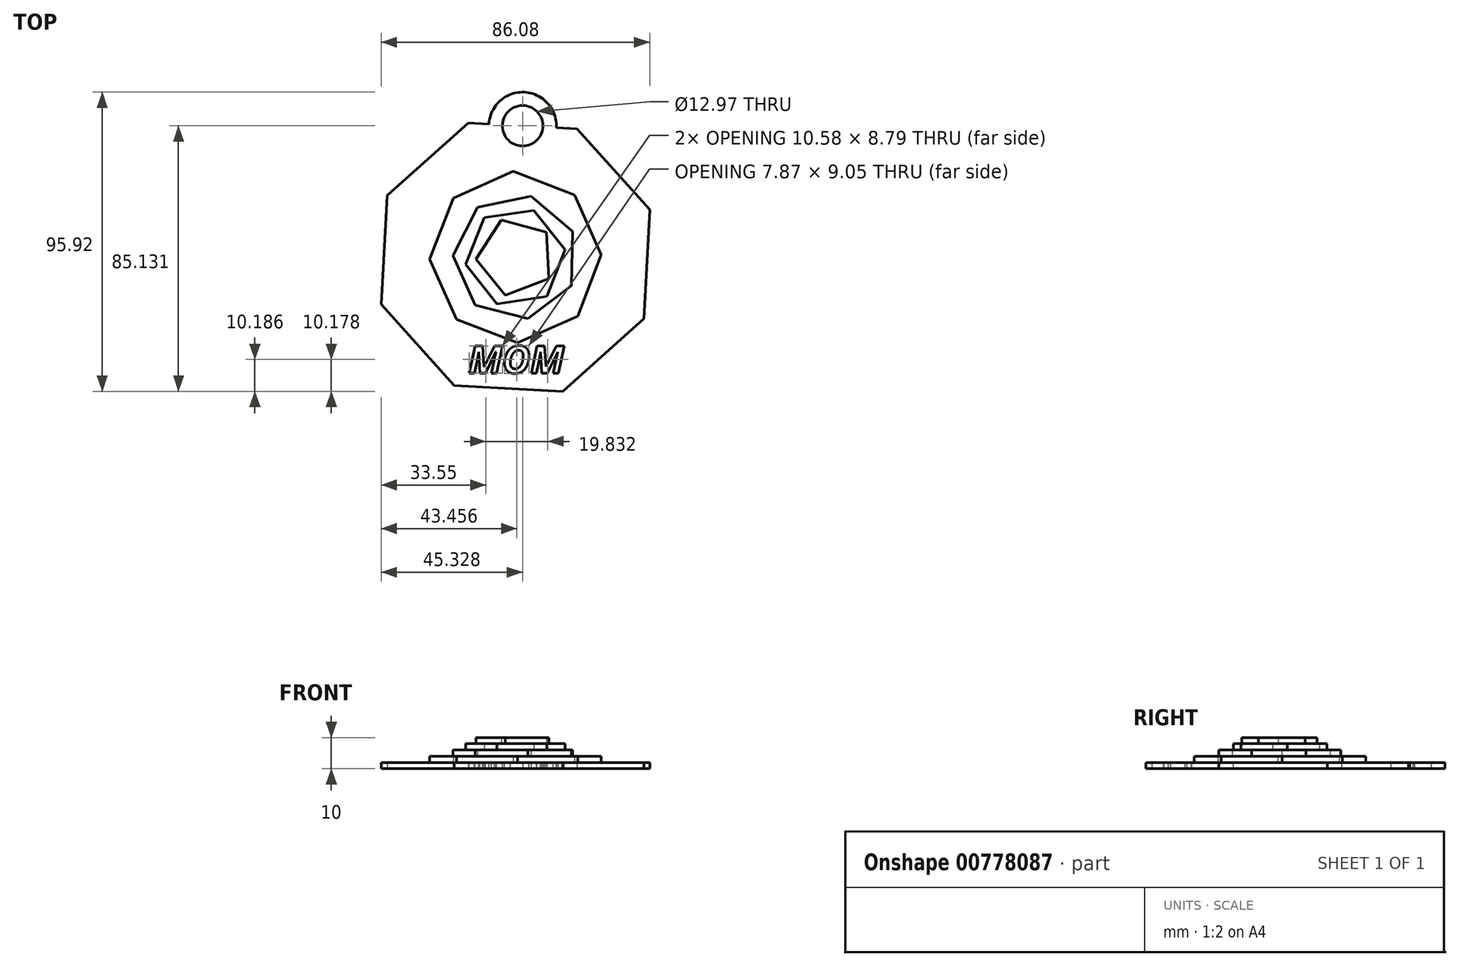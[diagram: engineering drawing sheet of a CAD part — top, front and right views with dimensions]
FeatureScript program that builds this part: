
annotation { "Feature Type Name" : "Feature", "Feature Type Description" : "" }
export const myFeature = defineFeature(function(context is Context, id is Id, definition is map)
    precondition{}
    {
        {
            var Q0;
            Q0=qCreatedBy(makeId("Top.planeOp"),FACE);
            var sketch = newSketch(context, id + "F0", { "sketchPlane" : qUnion([Q0])});
            skCircle(sketch, "E0.cCircle", {"center": v(0, 0) * mm, "radius": 42.15 * mm, "construction": true});
            skLineSegment(sketch, "E0.0", {"start": v(19.72, 41.14) * mm, "end": v(43.04, 15.15) * mm});
            skLineSegment(sketch, "E0.1", {"start": v(43.04, 15.15) * mm, "end": v(41.14, -19.72) * mm});
            skLineSegment(sketch, "E0.2", {"start": v(41.14, -19.72) * mm, "end": v(15.15, -43.04) * mm});
            skLineSegment(sketch, "E0.3", {"start": v(15.15, -43.04) * mm, "end": v(-19.72, -41.14) * mm});
            skLineSegment(sketch, "E0.4", {"start": v(-19.72, -41.14) * mm, "end": v(-43.04, -15.15) * mm});
            skLineSegment(sketch, "E0.5", {"start": v(-43.04, -15.15) * mm, "end": v(-41.14, 19.72) * mm});
            skLineSegment(sketch, "E0.6", {"start": v(-41.14, 19.72) * mm, "end": v(-15.15, 43.04) * mm});
            skLineSegment(sketch, "E0.7", {"start": v(-15.15, 43.04) * mm, "end": v(19.72, 41.14) * mm});
            skPoint(sketch, "E0.0.midPoint", {"position": v(31.38, 28.14) * mm});
            skSolve(sketch);
        }
        {
            var Q0;
            Q0=makeQuery(id+"F0.imprint","IMPRINT",FACE,{"disambiguationData":[TD([[makeQuery(id+"F0.imprint","IMPRINT",EDGE,{"derivedFrom":sQuery(id+"F0.wireOp",EDGE,"E0.0")}),-1.0]])]});
            extrude(context, id + "F1", {"entities" : qUnion([Q0]), "depth" : 2 * mm, "offsetDistance" : 25.4 * mm});
        }
        {
            var Q0;
            Q0=makeQuery(id+"F1.opExtrude","CAP_FACE",FACE,{"disambiguationData":[OSD([sQuery(id+"F0.wireOp",EDGE,"E0.0"),sQuery(id+"F0.wireOp",EDGE,"E0.1"),sQuery(id+"F0.wireOp",EDGE,"E0.2"),sQuery(id+"F0.wireOp",EDGE,"E0.3"),sQuery(id+"F0.wireOp",EDGE,"E0.4"),sQuery(id+"F0.wireOp",EDGE,"E0.5"),sQuery(id+"F0.wireOp",EDGE,"E0.6"),sQuery(id+"F0.wireOp",EDGE,"E0.7")])],"isStart":false});
            var sketch = newSketch(context, id + "F2", { "sketchPlane" : qUnion([Q0])});
            skCircle(sketch, "E1.cCircle", {"center": v(0, 0) * mm, "radius": 25.4 * mm, "construction": true});
            skLineSegment(sketch, "E1.0", {"start": v(-19.93, 18.95) * mm, "end": v(-0.7, 27.5) * mm});
            skLineSegment(sketch, "E1.1", {"start": v(-0.7, 27.5) * mm, "end": v(18.95, 19.93) * mm});
            skLineSegment(sketch, "E1.2", {"start": v(18.95, 19.93) * mm, "end": v(27.5, 0.7) * mm});
            skLineSegment(sketch, "E1.3", {"start": v(27.5, 0.7) * mm, "end": v(19.93, -18.95) * mm});
            skLineSegment(sketch, "E1.4", {"start": v(19.93, -18.95) * mm, "end": v(0.7, -27.5) * mm});
            skLineSegment(sketch, "E1.5", {"start": v(0.7, -27.5) * mm, "end": v(-18.95, -19.93) * mm});
            skLineSegment(sketch, "E1.6", {"start": v(-18.95, -19.93) * mm, "end": v(-27.5, -0.7) * mm});
            skLineSegment(sketch, "E1.7", {"start": v(-27.5, -0.7) * mm, "end": v(-19.93, 18.95) * mm});
            skPoint(sketch, "E1.0.midPoint", {"position": v(-10.31, 23.22) * mm});
            skSolve(sketch);
        }
        {
            var Q0;
            Q0=qSketchRegion(id+"F2",true);
            extrude(context, id + "F3", {"entities" : qUnion([Q0]), "operationType" : NewBodyOperationType.ADD, "depth" : 2 * mm, "offsetDistance" : 25.4 * mm});
        }
        {
            var Q0;
            Q0=makeQuery(id+"F3.opExtrude","CAP_FACE",FACE,{"disambiguationData":[OSD([sQuery(id+"F2.wireOp",EDGE,"E1.0"),sQuery(id+"F2.wireOp",EDGE,"E1.1"),sQuery(id+"F2.wireOp",EDGE,"E1.2"),sQuery(id+"F2.wireOp",EDGE,"E1.3"),sQuery(id+"F2.wireOp",EDGE,"E1.4"),sQuery(id+"F2.wireOp",EDGE,"E1.5"),sQuery(id+"F2.wireOp",EDGE,"E1.6"),sQuery(id+"F2.wireOp",EDGE,"E1.7")])],"isStart":false});
            var sketch = newSketch(context, id + "F4", { "sketchPlane" : qUnion([Q0])});
            skCircle(sketch, "E2.cCircle", {"center": v(0, 0) * mm, "radius": 18.1 * mm, "construction": true});
            skLineSegment(sketch, "E2.0", {"start": v(-20.08, 0.5) * mm, "end": v(-12.13, 16.02) * mm});
            skLineSegment(sketch, "E2.1", {"start": v(-12.13, 16.02) * mm, "end": v(4.96, 19.47) * mm});
            skLineSegment(sketch, "E2.2", {"start": v(4.96, 19.47) * mm, "end": v(18.32, 8.26) * mm});
            skLineSegment(sketch, "E2.3", {"start": v(18.32, 8.26) * mm, "end": v(17.87, -9.17) * mm});
            skLineSegment(sketch, "E2.4", {"start": v(17.87, -9.17) * mm, "end": v(3.97, -19.7) * mm});
            skLineSegment(sketch, "E2.5", {"start": v(3.97, -19.7) * mm, "end": v(-12.92, -15.39) * mm});
            skLineSegment(sketch, "E2.6", {"start": v(-12.92, -15.39) * mm, "end": v(-20.08, 0.5) * mm});
            skPoint(sketch, "E2.0.midPoint", {"position": v(-16.1, 8.26) * mm});
            skSolve(sketch);
        }
        {
            var Q0;
            Q0=qSketchRegion(id+"F4",true);
            extrude(context, id + "F5", {"entities" : qUnion([Q0]), "operationType" : NewBodyOperationType.ADD, "depth" : 2 * mm, "offsetDistance" : 25.4 * mm});
        }
        {
            var Q0;
            Q0=makeQuery(id+"F5.opExtrude","CAP_FACE",FACE,{"disambiguationData":[OSD([sQuery(id+"F4.wireOp",EDGE,"E2.0"),sQuery(id+"F4.wireOp",EDGE,"E2.1"),sQuery(id+"F4.wireOp",EDGE,"E2.2"),sQuery(id+"F4.wireOp",EDGE,"E2.3"),sQuery(id+"F4.wireOp",EDGE,"E2.4"),sQuery(id+"F4.wireOp",EDGE,"E2.5"),sQuery(id+"F4.wireOp",EDGE,"E2.6")])],"isStart":false});
            var sketch = newSketch(context, id + "F6", { "sketchPlane" : qUnion([Q0])});
            skSolve(sketch);
        }
        {
            var Q0;
            Q0=makeQuery(id+"F6.imprint","IMPRINT",FACE,{"disambiguationData":[TD([[makeQuery(id+"F6.imprint","IMPRINT",EDGE,{"derivedFrom":makeQuery(id+"F5.opExtrude","CAP_EDGE",EDGE,{"disambiguationData":[OSD([sQuery(id+"F4.wireOp",EDGE,"E2.0")])],"isStart":false})}),-1.0]])]});
            var sketch = newSketch(context, id + "F7", { "sketchPlane" : qUnion([Q0])});
            skCircle(sketch, "E3.cCircle", {"center": v(0, 0) * mm, "radius": 13.94 * mm, "construction": true});
            skLineSegment(sketch, "E3.0", {"start": v(-15.93, -2.36) * mm, "end": v(-10, 12.61) * mm});
            skLineSegment(sketch, "E3.1", {"start": v(-10, 12.61) * mm, "end": v(5.92, 14.97) * mm});
            skLineSegment(sketch, "E3.2", {"start": v(5.92, 14.97) * mm, "end": v(15.93, 2.36) * mm});
            skLineSegment(sketch, "E3.3", {"start": v(15.93, 2.36) * mm, "end": v(10, -12.61) * mm});
            skLineSegment(sketch, "E3.4", {"start": v(10, -12.61) * mm, "end": v(-5.92, -14.97) * mm});
            skLineSegment(sketch, "E3.5", {"start": v(-5.92, -14.97) * mm, "end": v(-15.93, -2.36) * mm});
            skPoint(sketch, "E3.0.midPoint", {"position": v(-12.97, 5.13) * mm});
            skSolve(sketch);
        }
        {
            var Q0;
            Q0=qSketchRegion(id+"F7",true);
            extrude(context, id + "F8", {"entities" : qUnion([Q0]), "operationType" : NewBodyOperationType.ADD, "depth" : 2 * mm, "offsetDistance" : 25.4 * mm});
        }
        {
            var Q0;
            Q0=makeQuery(id+"F8.opExtrude","CAP_FACE",FACE,{"disambiguationData":[OSD([sQuery(id+"F7.wireOp",EDGE,"E3.0"),sQuery(id+"F7.wireOp",EDGE,"E3.1"),sQuery(id+"F7.wireOp",EDGE,"E3.2"),sQuery(id+"F7.wireOp",EDGE,"E3.3"),sQuery(id+"F7.wireOp",EDGE,"E3.4"),sQuery(id+"F7.wireOp",EDGE,"E3.5")])],"isStart":false});
            var sketch = newSketch(context, id + "F9", { "sketchPlane" : qUnion([Q0])});
            skCircle(sketch, "E4.cCircle", {"center": v(0, 0) * mm, "radius": 10.29 * mm, "construction": true});
            skLineSegment(sketch, "E4.0", {"start": v(-12.7, -0.66) * mm, "end": v(-4.55, 11.88) * mm});
            skLineSegment(sketch, "E4.1", {"start": v(-4.55, 11.88) * mm, "end": v(9.89, 8) * mm});
            skLineSegment(sketch, "E4.2", {"start": v(9.89, 8) * mm, "end": v(10.66, -6.93) * mm});
            skLineSegment(sketch, "E4.3", {"start": v(10.66, -6.93) * mm, "end": v(-3.3, -12.28) * mm});
            skLineSegment(sketch, "E4.4", {"start": v(-3.3, -12.28) * mm, "end": v(-12.7, -0.66) * mm});
            skPoint(sketch, "E4.0.midPoint", {"position": v(-8.63, 5.6) * mm});
            skSolve(sketch);
        }
        {
            var Q0;
            Q0=qSketchRegion(id+"F9",true);
            extrude(context, id + "F10", {"entities" : qUnion([Q0]), "operationType" : NewBodyOperationType.ADD, "depth" : 2 * mm, "offsetDistance" : 25.4 * mm});
        }
        {
            var Q0;
            Q0=makeQuery(id+"F1.opExtrude","CAP_FACE",FACE,{"disambiguationData":[OSD([sQuery(id+"F0.wireOp",EDGE,"E0.0"),sQuery(id+"F0.wireOp",EDGE,"E0.1"),sQuery(id+"F0.wireOp",EDGE,"E0.2"),sQuery(id+"F0.wireOp",EDGE,"E0.3"),sQuery(id+"F0.wireOp",EDGE,"E0.4"),sQuery(id+"F0.wireOp",EDGE,"E0.5"),sQuery(id+"F0.wireOp",EDGE,"E0.6"),sQuery(id+"F0.wireOp",EDGE,"E0.7")])],"isStart":false});
            var sketch = newSketch(context, id + "F11", { "sketchPlane" : qUnion([Q0])});
            skCircle(sketch, "E5", {"center": v(2.29, 42.1) * mm, "radius": 10.8 * mm});
            skSolve(sketch);
        }
        {
            var Q0;
            Q0=qSketchRegion(id+"F11",true);
            extrude(context, id + "F12", {"entities" : qUnion([Q0]), "operationType" : NewBodyOperationType.ADD, "oppositeDirection" : true, "depth" : 2 * mm, "offsetDistance" : 25.4 * mm});
        }
        {
            var Q0;
            Q0=makeQuery(id+"F12.boolean.opBoolean","MERGE",FACE,{"derivedFrom":[makeQuery(id+"F1.opExtrude","CAP_FACE",FACE,{"disambiguationData":[OSD([sQuery(id+"F0.wireOp",EDGE,"E0.0"),sQuery(id+"F0.wireOp",EDGE,"E0.1"),sQuery(id+"F0.wireOp",EDGE,"E0.2"),sQuery(id+"F0.wireOp",EDGE,"E0.3"),sQuery(id+"F0.wireOp",EDGE,"E0.4"),sQuery(id+"F0.wireOp",EDGE,"E0.5"),sQuery(id+"F0.wireOp",EDGE,"E0.6"),sQuery(id+"F0.wireOp",EDGE,"E0.7")])],"isStart":false}),makeQuery(id+"F12.opExtrude","CAP_FACE",FACE,{"disambiguationData":[OSD([sQuery(id+"F11.wireOp",EDGE,"E5")])],"isStart":true})]});
            var sketch = newSketch(context, id + "F13", { "sketchPlane" : qUnion([Q0])});
            skCircle(sketch, "E6", {"center": v(2.29, 42.1) * mm, "radius": 6.48 * mm});
            skSolve(sketch);
        }
        {
            var Q0;
            Q0=qSketchRegion(id+"F13",true);
            extrude(context, id + "F14", {"entities" : qUnion([Q0]), "operationType" : NewBodyOperationType.REMOVE, "oppositeDirection" : true, "depth" : 25.4 * mm, "offsetDistance" : 25.4 * mm});
        }
        {
            var Q0;
            Q0=makeQuery(id+"F12.boolean.opBoolean","MERGE",FACE,{"derivedFrom":[makeQuery(id+"F1.opExtrude","CAP_FACE",FACE,{"disambiguationData":[OSD([sQuery(id+"F0.wireOp",EDGE,"E0.0"),sQuery(id+"F0.wireOp",EDGE,"E0.1"),sQuery(id+"F0.wireOp",EDGE,"E0.2"),sQuery(id+"F0.wireOp",EDGE,"E0.3"),sQuery(id+"F0.wireOp",EDGE,"E0.4"),sQuery(id+"F0.wireOp",EDGE,"E0.5"),sQuery(id+"F0.wireOp",EDGE,"E0.6"),sQuery(id+"F0.wireOp",EDGE,"E0.7")])],"isStart":false}),makeQuery(id+"F12.opExtrude","CAP_FACE",FACE,{"disambiguationData":[OSD([sQuery(id+"F11.wireOp",EDGE,"E5")])],"isStart":true})]});
            var sketch = newSketch(context, id + "F15", { "sketchPlane" : qUnion([Q0])});
            skText(sketch, "E7", { "text": "MOM", "fontName": "OpenSans-BoldItalic.ttf"});
            const initialGuessF15  = {"E7": [-0.0151, -0.03726, 1, 0, 0.00887]};
            skSetInitialGuess(sketch, initialGuessF15);
            skSolve(sketch);
        }
        {
            var Q0;
            Q0=qSketchRegion(id+"F15",true);
            extrude(context, id + "F16", {"entities" : qUnion([Q0]), "operationType" : NewBodyOperationType.REMOVE, "oppositeDirection" : true, "depth" : 25.4 * mm, "offsetDistance" : 25.4 * mm});
        }
    });
